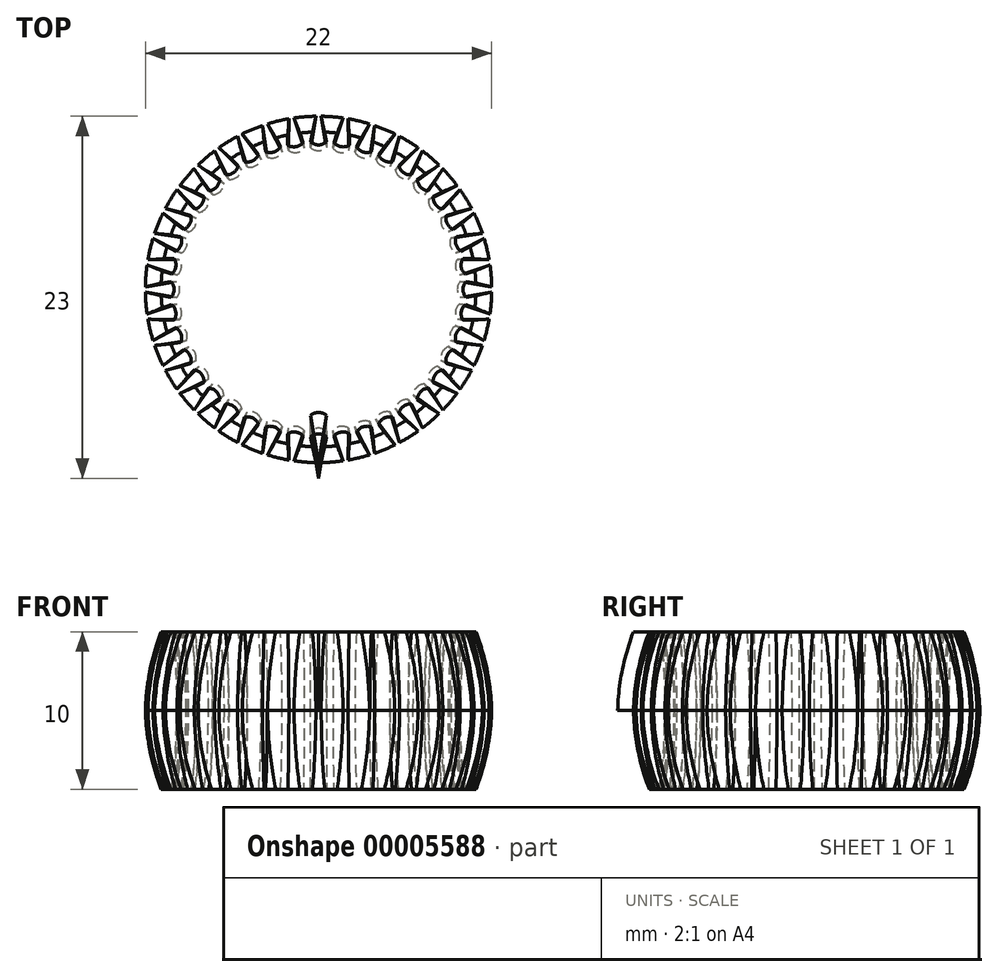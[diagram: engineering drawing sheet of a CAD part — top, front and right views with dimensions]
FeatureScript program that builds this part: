
annotation { "Feature Type Name" : "Feature", "Feature Type Description" : "" }
export const myFeature = defineFeature(function(context is Context, id is Id, definition is map)
    precondition{}
    {
        {
            var Q0;
            Q0=qCreatedBy(makeId("Right.planeOp"),FACE);
            var sketch = newSketch(context, id + "F0", { "sketchPlane" : qUnion([Q0])});
            skLineSegment(sketch, "E0.bottom", {"start": v(0, 5) * mm, "end": v(-10, 5) * mm});
            skLineSegment(sketch, "E0.left", {"start": v(0, 5) * mm, "end": v(0, 0) * mm});
            skLineSegment(sketch, "E1", {"start": v(-10, 5) * mm, "end": v(-10, 0) * mm, "construction": true});
            skArc(sketch, "E2", {"start": v(-10, 5) * mm, "mid": v(-10.71, 2.54) * mm, "end": v(-11, 0) * mm});
            skPoint(sketch, "E2.third.point", {"position": v(13.48, -12.02) * mm});
            skLineSegment(sketch, "E3", {"start": v(-11, 0) * mm, "end": v(0, 0) * mm});
            skSolve(sketch);
        }
        {
            var Q0;
            Q0=makeQuery(id+"F0.imprint","IMPRINT",FACE,{"disambiguationData":[TD([[makeQuery(id+"F0.imprint","IMPRINT",EDGE,{"derivedFrom":sQuery(id+"F0.wireOp",EDGE,"E0.bottom")}),1.0]])]});
            var Q1;
            Q1=sQuery(id+"F0.wireOp",EDGE,"E0.left");
            revolve(context, id + "F1", {"entities" : qUnion([Q0]), "axis" : qUnion([Q1]), "revolveType" : RevolveType.FULL});
        }
        {
            var Q0;
            Q0=qCreatedBy(makeId("Top.planeOp"),FACE);
            var sketch = newSketch(context, id + "F2", { "sketchPlane" : qUnion([Q0])});
            skLineSegment(sketch, "E4", {"start": v(0, -12) * mm, "end": v(-0.5, -9) * mm});
            skLineSegment(sketch, "E5", {"start": v(-0.5, -9) * mm, "end": v(0, -9) * mm});
            skLineSegment(sketch, "E6.0.MirrorCS", {"start": v(0, -12) * mm, "end": v(0.5, -9) * mm});
            skLineSegment(sketch, "E6.1.MirrorCS", {"start": v(0.5, -9) * mm, "end": v(0, -9) * mm});
            skLineSegment(sketch, "E7", {"start": v(0, 0) * mm, "end": v(0, -12) * mm, "construction": true});
            skLineSegment(sketch, "E8", {"start": v(0, -12) * mm, "end": v(0, -9) * mm, "construction": true});
            skArc(sketch, "E9", {"start": v(0.5, -9) * mm, "mid": v(0, -8.81) * mm, "end": v(-0.5, -9) * mm});
            skSolve(sketch);
        }
        {
            var Q0;
            Q0=qCreatedBy(makeId("Right.planeOp"),FACE);
            var sketch = newSketch(context, id + "F3", { "sketchPlane" : qUnion([Q0])});
            skFitSpline(sketch, "E10", {"points": [v(-9.63, 0) * mm, v(-10, 5) * mm], "startDerivative": vector(-0.08, 3.63) * mm, "endDerivative": vector(-0.92, 4.07) * mm});
            skSolve(sketch);
        }
        {
            var Q0;
            Q0 = qSketchRegion(id + "F2", true);
            var Q1;
            Q1=sQuery(id+"F0.wireOp",EDGE,"E2");
            sweep(context, id + "F4", {"profiles" : qUnion([Q0]), "path" : qUnion([Q1]), "keepProfileOrientation" : true});
        }
        {
            var Q0;
            Q0=qCreatedBy(makeId("Right.planeOp"),FACE);
            var sketch = newSketch(context, id + "F5", { "sketchPlane" : qUnion([Q0])});
            skLineSegment(sketch, "E11", {"start": v(0, 0) * mm, "end": v(0, 14.13) * mm, "construction": true});
            skSolve(sketch);
        }
        {
            var Q0;
            Q0 = qSketchRegion(id + "F2", true);
            var Q1;
            Q1 = qBodyType(qCreatedBy(id + "F3" ,EDGE), BodyType.WIRE);
            sweep(context, id + "F6", {"profiles" : qUnion([Q0]), "path" : qUnion([Q1]), "keepProfileOrientation" : true});
        }
        {
            var Q0;
            Q0=makeQuery(id+"F4.opSweep","SWEPT_FACE",FACE,{"disambiguationData":[OSD([sQuery(id+"F0.wireOp",EDGE,"E2"),sQuery(id+"F2.wireOp",EDGE,"E6.0.MirrorCS")])]});
            var Q1;
            Q1=makeQuery(id+"F6.opSweep","SWEPT_BODY",BODY,{"disambiguationData":[OSD([sQuery(id+"F0.wireOp",EDGE,"E1"),sQuery(id+"F2.wireOp",EDGE,"E4"),sQuery(id+"F2.wireOp",EDGE,"E6.0.MirrorCS"),sQuery(id+"F2.wireOp",EDGE,"E9")])]});
            var Q2;
            Q2=sQuery(id+"F5.wireOp",EDGE,"E11");
            circularPattern(context, id + "F7", {"entities" : qUnion([Q1]), "axis" : qUnion([Q2]), "angle" : 360 * degree, "instanceCount" : 40, "equalSpace" : true});
        }
        {
            var Q0;
            Q0=makeQuery(id+"F7.opPattern","COPY",BODY,{"derivedFrom":makeQuery(id+"F6.opSweep","SWEPT_BODY",BODY,{"disambiguationData":[OSD([sQuery(id+"F0.wireOp",EDGE,"E1"),sQuery(id+"F2.wireOp",EDGE,"E4"),sQuery(id+"F2.wireOp",EDGE,"E6.0.MirrorCS"),sQuery(id+"F2.wireOp",EDGE,"E9")])]}),"instanceName":"22"});
            var Q1;
            Q1=makeQuery(id+"F7.opPattern","COPY",BODY,{"derivedFrom":makeQuery(id+"F6.opSweep","SWEPT_BODY",BODY,{"disambiguationData":[OSD([sQuery(id+"F0.wireOp",EDGE,"E1"),sQuery(id+"F2.wireOp",EDGE,"E4"),sQuery(id+"F2.wireOp",EDGE,"E6.0.MirrorCS"),sQuery(id+"F2.wireOp",EDGE,"E9")])]}),"instanceName":"18"});
            var Q2;
            Q2=makeQuery(id+"F7.opPattern","COPY",BODY,{"derivedFrom":makeQuery(id+"F6.opSweep","SWEPT_BODY",BODY,{"disambiguationData":[OSD([sQuery(id+"F0.wireOp",EDGE,"E1"),sQuery(id+"F2.wireOp",EDGE,"E4"),sQuery(id+"F2.wireOp",EDGE,"E6.0.MirrorCS"),sQuery(id+"F2.wireOp",EDGE,"E9")])]}),"instanceName":"43"});
            var Q3;
            Q3=makeQuery(id+"F7.opPattern","COPY",BODY,{"derivedFrom":makeQuery(id+"F6.opSweep","SWEPT_BODY",BODY,{"disambiguationData":[OSD([sQuery(id+"F0.wireOp",EDGE,"E1"),sQuery(id+"F2.wireOp",EDGE,"E4"),sQuery(id+"F2.wireOp",EDGE,"E6.0.MirrorCS"),sQuery(id+"F2.wireOp",EDGE,"E9")])]}),"instanceName":"26"});
            var Q4;
            Q4=makeQuery(id+"F7.opPattern","COPY",BODY,{"derivedFrom":makeQuery(id+"F6.opSweep","SWEPT_BODY",BODY,{"disambiguationData":[OSD([sQuery(id+"F0.wireOp",EDGE,"E1"),sQuery(id+"F2.wireOp",EDGE,"E4"),sQuery(id+"F2.wireOp",EDGE,"E6.0.MirrorCS"),sQuery(id+"F2.wireOp",EDGE,"E9")])]}),"instanceName":"35"});
            var Q5;
            Q5=makeQuery(id+"F7.opPattern","COPY",BODY,{"derivedFrom":makeQuery(id+"F6.opSweep","SWEPT_BODY",BODY,{"disambiguationData":[OSD([sQuery(id+"F0.wireOp",EDGE,"E1"),sQuery(id+"F2.wireOp",EDGE,"E4"),sQuery(id+"F2.wireOp",EDGE,"E6.0.MirrorCS"),sQuery(id+"F2.wireOp",EDGE,"E9")])]}),"instanceName":"15"});
            var Q6;
            Q6=makeQuery(id+"F7.opPattern","COPY",BODY,{"derivedFrom":makeQuery(id+"F6.opSweep","SWEPT_BODY",BODY,{"disambiguationData":[OSD([sQuery(id+"F0.wireOp",EDGE,"E1"),sQuery(id+"F2.wireOp",EDGE,"E4"),sQuery(id+"F2.wireOp",EDGE,"E6.0.MirrorCS"),sQuery(id+"F2.wireOp",EDGE,"E9")])]}),"instanceName":"25"});
            var Q7;
            Q7=makeQuery(id+"F7.opPattern","COPY",BODY,{"derivedFrom":makeQuery(id+"F6.opSweep","SWEPT_BODY",BODY,{"disambiguationData":[OSD([sQuery(id+"F0.wireOp",EDGE,"E1"),sQuery(id+"F2.wireOp",EDGE,"E4"),sQuery(id+"F2.wireOp",EDGE,"E6.0.MirrorCS"),sQuery(id+"F2.wireOp",EDGE,"E9")])]}),"instanceName":"39"});
            var Q8;
            Q8=makeQuery(id+"F7.opPattern","COPY",BODY,{"derivedFrom":makeQuery(id+"F6.opSweep","SWEPT_BODY",BODY,{"disambiguationData":[OSD([sQuery(id+"F0.wireOp",EDGE,"E1"),sQuery(id+"F2.wireOp",EDGE,"E4"),sQuery(id+"F2.wireOp",EDGE,"E6.0.MirrorCS"),sQuery(id+"F2.wireOp",EDGE,"E9")])]}),"instanceName":"42"});
            var Q9;
            Q9=makeQuery(id+"F7.opPattern","COPY",BODY,{"derivedFrom":makeQuery(id+"F6.opSweep","SWEPT_BODY",BODY,{"disambiguationData":[OSD([sQuery(id+"F0.wireOp",EDGE,"E1"),sQuery(id+"F2.wireOp",EDGE,"E4"),sQuery(id+"F2.wireOp",EDGE,"E6.0.MirrorCS"),sQuery(id+"F2.wireOp",EDGE,"E9")])]}),"instanceName":"40"});
            var Q10;
            Q10=makeQuery(id+"F7.opPattern","COPY",BODY,{"derivedFrom":makeQuery(id+"F6.opSweep","SWEPT_BODY",BODY,{"disambiguationData":[OSD([sQuery(id+"F0.wireOp",EDGE,"E1"),sQuery(id+"F2.wireOp",EDGE,"E4"),sQuery(id+"F2.wireOp",EDGE,"E6.0.MirrorCS"),sQuery(id+"F2.wireOp",EDGE,"E9")])]}),"instanceName":"16"});
            var Q11;
            Q11=makeQuery(id+"F7.opPattern","COPY",BODY,{"derivedFrom":makeQuery(id+"F6.opSweep","SWEPT_BODY",BODY,{"disambiguationData":[OSD([sQuery(id+"F0.wireOp",EDGE,"E1"),sQuery(id+"F2.wireOp",EDGE,"E4"),sQuery(id+"F2.wireOp",EDGE,"E6.0.MirrorCS"),sQuery(id+"F2.wireOp",EDGE,"E9")])]}),"instanceName":"33"});
            var Q12;
            Q12=makeQuery(id+"F7.opPattern","COPY",BODY,{"derivedFrom":makeQuery(id+"F6.opSweep","SWEPT_BODY",BODY,{"disambiguationData":[OSD([sQuery(id+"F0.wireOp",EDGE,"E1"),sQuery(id+"F2.wireOp",EDGE,"E4"),sQuery(id+"F2.wireOp",EDGE,"E6.0.MirrorCS"),sQuery(id+"F2.wireOp",EDGE,"E9")])]}),"instanceName":"45"});
            var Q13;
            Q13=makeQuery(id+"F7.opPattern","COPY",BODY,{"derivedFrom":makeQuery(id+"F6.opSweep","SWEPT_BODY",BODY,{"disambiguationData":[OSD([sQuery(id+"F0.wireOp",EDGE,"E1"),sQuery(id+"F2.wireOp",EDGE,"E4"),sQuery(id+"F2.wireOp",EDGE,"E6.0.MirrorCS"),sQuery(id+"F2.wireOp",EDGE,"E9")])]}),"instanceName":"32"});
            var Q14;
            Q14=makeQuery(id+"F7.opPattern","COPY",BODY,{"derivedFrom":makeQuery(id+"F6.opSweep","SWEPT_BODY",BODY,{"disambiguationData":[OSD([sQuery(id+"F0.wireOp",EDGE,"E1"),sQuery(id+"F2.wireOp",EDGE,"E4"),sQuery(id+"F2.wireOp",EDGE,"E6.0.MirrorCS"),sQuery(id+"F2.wireOp",EDGE,"E9")])]}),"instanceName":"4"});
            var Q15;
            Q15=makeQuery(id+"F7.opPattern","COPY",BODY,{"derivedFrom":makeQuery(id+"F6.opSweep","SWEPT_BODY",BODY,{"disambiguationData":[OSD([sQuery(id+"F0.wireOp",EDGE,"E1"),sQuery(id+"F2.wireOp",EDGE,"E4"),sQuery(id+"F2.wireOp",EDGE,"E6.0.MirrorCS"),sQuery(id+"F2.wireOp",EDGE,"E9")])]}),"instanceName":"29"});
            var Q16;
            Q16=makeQuery(id+"F7.opPattern","COPY",BODY,{"derivedFrom":makeQuery(id+"F6.opSweep","SWEPT_BODY",BODY,{"disambiguationData":[OSD([sQuery(id+"F0.wireOp",EDGE,"E1"),sQuery(id+"F2.wireOp",EDGE,"E4"),sQuery(id+"F2.wireOp",EDGE,"E6.0.MirrorCS"),sQuery(id+"F2.wireOp",EDGE,"E9")])]}),"instanceName":"7"});
            var Q17;
            Q17=makeQuery(id+"F7.opPattern","COPY",BODY,{"derivedFrom":makeQuery(id+"F6.opSweep","SWEPT_BODY",BODY,{"disambiguationData":[OSD([sQuery(id+"F0.wireOp",EDGE,"E1"),sQuery(id+"F2.wireOp",EDGE,"E4"),sQuery(id+"F2.wireOp",EDGE,"E6.0.MirrorCS"),sQuery(id+"F2.wireOp",EDGE,"E9")])]}),"instanceName":"14"});
            var Q18;
            Q18=makeQuery(id+"F7.opPattern","COPY",BODY,{"derivedFrom":makeQuery(id+"F6.opSweep","SWEPT_BODY",BODY,{"disambiguationData":[OSD([sQuery(id+"F0.wireOp",EDGE,"E1"),sQuery(id+"F2.wireOp",EDGE,"E4"),sQuery(id+"F2.wireOp",EDGE,"E6.0.MirrorCS"),sQuery(id+"F2.wireOp",EDGE,"E9")])]}),"instanceName":"48"});
            var Q19;
            Q19=makeQuery(id+"F7.opPattern","COPY",BODY,{"derivedFrom":makeQuery(id+"F6.opSweep","SWEPT_BODY",BODY,{"disambiguationData":[OSD([sQuery(id+"F0.wireOp",EDGE,"E1"),sQuery(id+"F2.wireOp",EDGE,"E4"),sQuery(id+"F2.wireOp",EDGE,"E6.0.MirrorCS"),sQuery(id+"F2.wireOp",EDGE,"E9")])]}),"instanceName":"11"});
            var Q20;
            Q20=makeQuery(id+"F7.opPattern","COPY",BODY,{"derivedFrom":makeQuery(id+"F6.opSweep","SWEPT_BODY",BODY,{"disambiguationData":[OSD([sQuery(id+"F0.wireOp",EDGE,"E1"),sQuery(id+"F2.wireOp",EDGE,"E4"),sQuery(id+"F2.wireOp",EDGE,"E6.0.MirrorCS"),sQuery(id+"F2.wireOp",EDGE,"E9")])]}),"instanceName":"12"});
            var Q21;
            Q21=makeQuery(id+"F7.opPattern","COPY",BODY,{"derivedFrom":makeQuery(id+"F6.opSweep","SWEPT_BODY",BODY,{"disambiguationData":[OSD([sQuery(id+"F0.wireOp",EDGE,"E1"),sQuery(id+"F2.wireOp",EDGE,"E4"),sQuery(id+"F2.wireOp",EDGE,"E6.0.MirrorCS"),sQuery(id+"F2.wireOp",EDGE,"E9")])]}),"instanceName":"37"});
            var Q22;
            Q22=makeQuery(id+"F7.opPattern","COPY",BODY,{"derivedFrom":makeQuery(id+"F6.opSweep","SWEPT_BODY",BODY,{"disambiguationData":[OSD([sQuery(id+"F0.wireOp",EDGE,"E1"),sQuery(id+"F2.wireOp",EDGE,"E4"),sQuery(id+"F2.wireOp",EDGE,"E6.0.MirrorCS"),sQuery(id+"F2.wireOp",EDGE,"E9")])]}),"instanceName":"44"});
            var Q23;
            Q23=makeQuery(id+"F6.opSweep","SWEPT_BODY",BODY,{"disambiguationData":[OSD([sQuery(id+"F0.wireOp",EDGE,"E1"),sQuery(id+"F2.wireOp",EDGE,"E4"),sQuery(id+"F2.wireOp",EDGE,"E6.0.MirrorCS"),sQuery(id+"F2.wireOp",EDGE,"E9")])]});
            var Q24;
            Q24=makeQuery(id+"F7.opPattern","COPY",BODY,{"derivedFrom":makeQuery(id+"F6.opSweep","SWEPT_BODY",BODY,{"disambiguationData":[OSD([sQuery(id+"F0.wireOp",EDGE,"E1"),sQuery(id+"F2.wireOp",EDGE,"E4"),sQuery(id+"F2.wireOp",EDGE,"E6.0.MirrorCS"),sQuery(id+"F2.wireOp",EDGE,"E9")])]}),"instanceName":"9"});
            var Q25;
            Q25=makeQuery(id+"F7.opPattern","COPY",BODY,{"derivedFrom":makeQuery(id+"F6.opSweep","SWEPT_BODY",BODY,{"disambiguationData":[OSD([sQuery(id+"F0.wireOp",EDGE,"E1"),sQuery(id+"F2.wireOp",EDGE,"E4"),sQuery(id+"F2.wireOp",EDGE,"E6.0.MirrorCS"),sQuery(id+"F2.wireOp",EDGE,"E9")])]}),"instanceName":"10"});
            var Q26;
            Q26=makeQuery(id+"F7.opPattern","COPY",BODY,{"derivedFrom":makeQuery(id+"F6.opSweep","SWEPT_BODY",BODY,{"disambiguationData":[OSD([sQuery(id+"F0.wireOp",EDGE,"E1"),sQuery(id+"F2.wireOp",EDGE,"E4"),sQuery(id+"F2.wireOp",EDGE,"E6.0.MirrorCS"),sQuery(id+"F2.wireOp",EDGE,"E9")])]}),"instanceName":"20"});
            var Q27;
            Q27=makeQuery(id+"F7.opPattern","COPY",BODY,{"derivedFrom":makeQuery(id+"F6.opSweep","SWEPT_BODY",BODY,{"disambiguationData":[OSD([sQuery(id+"F0.wireOp",EDGE,"E1"),sQuery(id+"F2.wireOp",EDGE,"E4"),sQuery(id+"F2.wireOp",EDGE,"E6.0.MirrorCS"),sQuery(id+"F2.wireOp",EDGE,"E9")])]}),"instanceName":"47"});
            var Q28;
            Q28=makeQuery(id+"F7.opPattern","COPY",BODY,{"derivedFrom":makeQuery(id+"F6.opSweep","SWEPT_BODY",BODY,{"disambiguationData":[OSD([sQuery(id+"F0.wireOp",EDGE,"E1"),sQuery(id+"F2.wireOp",EDGE,"E4"),sQuery(id+"F2.wireOp",EDGE,"E6.0.MirrorCS"),sQuery(id+"F2.wireOp",EDGE,"E9")])]}),"instanceName":"6"});
            var Q29;
            Q29=makeQuery(id+"F7.opPattern","COPY",BODY,{"derivedFrom":makeQuery(id+"F6.opSweep","SWEPT_BODY",BODY,{"disambiguationData":[OSD([sQuery(id+"F0.wireOp",EDGE,"E1"),sQuery(id+"F2.wireOp",EDGE,"E4"),sQuery(id+"F2.wireOp",EDGE,"E6.0.MirrorCS"),sQuery(id+"F2.wireOp",EDGE,"E9")])]}),"instanceName":"41"});
            var Q30;
            Q30=makeQuery(id+"F7.opPattern","COPY",BODY,{"derivedFrom":makeQuery(id+"F6.opSweep","SWEPT_BODY",BODY,{"disambiguationData":[OSD([sQuery(id+"F0.wireOp",EDGE,"E1"),sQuery(id+"F2.wireOp",EDGE,"E4"),sQuery(id+"F2.wireOp",EDGE,"E6.0.MirrorCS"),sQuery(id+"F2.wireOp",EDGE,"E9")])]}),"instanceName":"8"});
            var Q31;
            Q31=makeQuery(id+"F7.opPattern","COPY",BODY,{"derivedFrom":makeQuery(id+"F6.opSweep","SWEPT_BODY",BODY,{"disambiguationData":[OSD([sQuery(id+"F0.wireOp",EDGE,"E1"),sQuery(id+"F2.wireOp",EDGE,"E4"),sQuery(id+"F2.wireOp",EDGE,"E6.0.MirrorCS"),sQuery(id+"F2.wireOp",EDGE,"E9")])]}),"instanceName":"2"});
            var Q32;
            Q32=makeQuery(id+"F7.opPattern","COPY",BODY,{"derivedFrom":makeQuery(id+"F6.opSweep","SWEPT_BODY",BODY,{"disambiguationData":[OSD([sQuery(id+"F0.wireOp",EDGE,"E1"),sQuery(id+"F2.wireOp",EDGE,"E4"),sQuery(id+"F2.wireOp",EDGE,"E6.0.MirrorCS"),sQuery(id+"F2.wireOp",EDGE,"E9")])]}),"instanceName":"21"});
            var Q33;
            Q33=makeQuery(id+"F7.opPattern","COPY",BODY,{"derivedFrom":makeQuery(id+"F6.opSweep","SWEPT_BODY",BODY,{"disambiguationData":[OSD([sQuery(id+"F0.wireOp",EDGE,"E1"),sQuery(id+"F2.wireOp",EDGE,"E4"),sQuery(id+"F2.wireOp",EDGE,"E6.0.MirrorCS"),sQuery(id+"F2.wireOp",EDGE,"E9")])]}),"instanceName":"27"});
            var Q34;
            Q34=makeQuery(id+"F7.opPattern","COPY",BODY,{"derivedFrom":makeQuery(id+"F6.opSweep","SWEPT_BODY",BODY,{"disambiguationData":[OSD([sQuery(id+"F0.wireOp",EDGE,"E1"),sQuery(id+"F2.wireOp",EDGE,"E4"),sQuery(id+"F2.wireOp",EDGE,"E6.0.MirrorCS"),sQuery(id+"F2.wireOp",EDGE,"E9")])]}),"instanceName":"34"});
            var Q35;
            Q35=makeQuery(id+"F7.opPattern","COPY",BODY,{"derivedFrom":makeQuery(id+"F6.opSweep","SWEPT_BODY",BODY,{"disambiguationData":[OSD([sQuery(id+"F0.wireOp",EDGE,"E1"),sQuery(id+"F2.wireOp",EDGE,"E4"),sQuery(id+"F2.wireOp",EDGE,"E6.0.MirrorCS"),sQuery(id+"F2.wireOp",EDGE,"E9")])]}),"instanceName":"36"});
            var Q36;
            Q36=makeQuery(id+"F7.opPattern","COPY",BODY,{"derivedFrom":makeQuery(id+"F6.opSweep","SWEPT_BODY",BODY,{"disambiguationData":[OSD([sQuery(id+"F0.wireOp",EDGE,"E1"),sQuery(id+"F2.wireOp",EDGE,"E4"),sQuery(id+"F2.wireOp",EDGE,"E6.0.MirrorCS"),sQuery(id+"F2.wireOp",EDGE,"E9")])]}),"instanceName":"3"});
            var Q37;
            Q37=makeQuery(id+"F7.opPattern","COPY",BODY,{"derivedFrom":makeQuery(id+"F6.opSweep","SWEPT_BODY",BODY,{"disambiguationData":[OSD([sQuery(id+"F0.wireOp",EDGE,"E1"),sQuery(id+"F2.wireOp",EDGE,"E4"),sQuery(id+"F2.wireOp",EDGE,"E6.0.MirrorCS"),sQuery(id+"F2.wireOp",EDGE,"E9")])]}),"instanceName":"17"});
            var Q38;
            Q38=makeQuery(id+"F7.opPattern","COPY",BODY,{"derivedFrom":makeQuery(id+"F6.opSweep","SWEPT_BODY",BODY,{"disambiguationData":[OSD([sQuery(id+"F0.wireOp",EDGE,"E1"),sQuery(id+"F2.wireOp",EDGE,"E4"),sQuery(id+"F2.wireOp",EDGE,"E6.0.MirrorCS"),sQuery(id+"F2.wireOp",EDGE,"E9")])]}),"instanceName":"1"});
            var Q39;
            Q39=makeQuery(id+"F7.opPattern","COPY",BODY,{"derivedFrom":makeQuery(id+"F6.opSweep","SWEPT_BODY",BODY,{"disambiguationData":[OSD([sQuery(id+"F0.wireOp",EDGE,"E1"),sQuery(id+"F2.wireOp",EDGE,"E4"),sQuery(id+"F2.wireOp",EDGE,"E6.0.MirrorCS"),sQuery(id+"F2.wireOp",EDGE,"E9")])]}),"instanceName":"38"});
            var Q40;
            Q40=makeQuery(id+"F7.opPattern","COPY",BODY,{"derivedFrom":makeQuery(id+"F6.opSweep","SWEPT_BODY",BODY,{"disambiguationData":[OSD([sQuery(id+"F0.wireOp",EDGE,"E1"),sQuery(id+"F2.wireOp",EDGE,"E4"),sQuery(id+"F2.wireOp",EDGE,"E6.0.MirrorCS"),sQuery(id+"F2.wireOp",EDGE,"E9")])]}),"instanceName":"31"});
            var Q41;
            Q41=makeQuery(id+"F7.opPattern","COPY",BODY,{"derivedFrom":makeQuery(id+"F6.opSweep","SWEPT_BODY",BODY,{"disambiguationData":[OSD([sQuery(id+"F0.wireOp",EDGE,"E1"),sQuery(id+"F2.wireOp",EDGE,"E4"),sQuery(id+"F2.wireOp",EDGE,"E6.0.MirrorCS"),sQuery(id+"F2.wireOp",EDGE,"E9")])]}),"instanceName":"24"});
            var Q42;
            Q42=makeQuery(id+"F7.opPattern","COPY",BODY,{"derivedFrom":makeQuery(id+"F6.opSweep","SWEPT_BODY",BODY,{"disambiguationData":[OSD([sQuery(id+"F0.wireOp",EDGE,"E1"),sQuery(id+"F2.wireOp",EDGE,"E4"),sQuery(id+"F2.wireOp",EDGE,"E6.0.MirrorCS"),sQuery(id+"F2.wireOp",EDGE,"E9")])]}),"instanceName":"28"});
            var Q43;
            Q43=makeQuery(id+"F7.opPattern","COPY",BODY,{"derivedFrom":makeQuery(id+"F6.opSweep","SWEPT_BODY",BODY,{"disambiguationData":[OSD([sQuery(id+"F0.wireOp",EDGE,"E1"),sQuery(id+"F2.wireOp",EDGE,"E4"),sQuery(id+"F2.wireOp",EDGE,"E6.0.MirrorCS"),sQuery(id+"F2.wireOp",EDGE,"E9")])]}),"instanceName":"5"});
            var Q44;
            Q44=makeQuery(id+"F7.opPattern","COPY",BODY,{"derivedFrom":makeQuery(id+"F6.opSweep","SWEPT_BODY",BODY,{"disambiguationData":[OSD([sQuery(id+"F0.wireOp",EDGE,"E1"),sQuery(id+"F2.wireOp",EDGE,"E4"),sQuery(id+"F2.wireOp",EDGE,"E6.0.MirrorCS"),sQuery(id+"F2.wireOp",EDGE,"E9")])]}),"instanceName":"13"});
            var Q45;
            Q45=makeQuery(id+"F7.opPattern","COPY",BODY,{"derivedFrom":makeQuery(id+"F6.opSweep","SWEPT_BODY",BODY,{"disambiguationData":[OSD([sQuery(id+"F0.wireOp",EDGE,"E1"),sQuery(id+"F2.wireOp",EDGE,"E4"),sQuery(id+"F2.wireOp",EDGE,"E6.0.MirrorCS"),sQuery(id+"F2.wireOp",EDGE,"E9")])]}),"instanceName":"30"});
            var Q46;
            Q46=makeQuery(id+"F7.opPattern","COPY",BODY,{"derivedFrom":makeQuery(id+"F6.opSweep","SWEPT_BODY",BODY,{"disambiguationData":[OSD([sQuery(id+"F0.wireOp",EDGE,"E1"),sQuery(id+"F2.wireOp",EDGE,"E4"),sQuery(id+"F2.wireOp",EDGE,"E6.0.MirrorCS"),sQuery(id+"F2.wireOp",EDGE,"E9")])]}),"instanceName":"46"});
            var Q47;
            Q47=makeQuery(id+"F7.opPattern","COPY",BODY,{"derivedFrom":makeQuery(id+"F6.opSweep","SWEPT_BODY",BODY,{"disambiguationData":[OSD([sQuery(id+"F0.wireOp",EDGE,"E1"),sQuery(id+"F2.wireOp",EDGE,"E4"),sQuery(id+"F2.wireOp",EDGE,"E6.0.MirrorCS"),sQuery(id+"F2.wireOp",EDGE,"E9")])]}),"instanceName":"19"});
            var Q48;
            Q48=makeQuery(id+"F7.opPattern","COPY",BODY,{"derivedFrom":makeQuery(id+"F6.opSweep","SWEPT_BODY",BODY,{"disambiguationData":[OSD([sQuery(id+"F0.wireOp",EDGE,"E1"),sQuery(id+"F2.wireOp",EDGE,"E4"),sQuery(id+"F2.wireOp",EDGE,"E6.0.MirrorCS"),sQuery(id+"F2.wireOp",EDGE,"E9")])]}),"instanceName":"49"});
            var Q49;
            Q49=makeQuery(id+"F7.opPattern","COPY",BODY,{"derivedFrom":makeQuery(id+"F6.opSweep","SWEPT_BODY",BODY,{"disambiguationData":[OSD([sQuery(id+"F0.wireOp",EDGE,"E1"),sQuery(id+"F2.wireOp",EDGE,"E4"),sQuery(id+"F2.wireOp",EDGE,"E6.0.MirrorCS"),sQuery(id+"F2.wireOp",EDGE,"E9")])]}),"instanceName":"23"});
            var Q50;
            Q50=makeQuery(id+"F1.opRevolve","SWEPT_BODY",BODY,{"disambiguationData":[OSD([sQuery(id+"F0.wireOp",EDGE,"E0.bottom"),sQuery(id+"F0.wireOp",EDGE,"E0.left"),sQuery(id+"F0.wireOp",EDGE,"E2"),sQuery(id+"F0.wireOp",EDGE,"E3")])]});
            booleanBodies(context, id + "F8", {"operationType" : BooleanOperationType.SUBTRACTION, "tools" : qUnion([Q0, Q1, Q2, Q3, Q4, Q5, Q6, Q7, Q8, Q9, Q10, Q11, Q12, Q13, Q14, Q15, Q16, Q17, Q18, Q19, Q20, Q21, Q22, Q23, Q24, Q25, Q26, Q27, Q28, Q29, Q30, Q31, Q32, Q33, Q34, Q35, Q36, Q37, Q38, Q39, Q40, Q41, Q42, Q43, Q44, Q45, Q46, Q47, Q48, Q49]), "targets" : qUnion([Q50])});
        }
        {
            var Q0;
            Q0=makeQuery(id+"F1.opRevolve","SWEPT_BODY",BODY,{"disambiguationData":[OSD([sQuery(id+"F0.wireOp",EDGE,"E0.bottom"),sQuery(id+"F0.wireOp",EDGE,"E0.left"),sQuery(id+"F0.wireOp",EDGE,"E2"),sQuery(id+"F0.wireOp",EDGE,"E3")])]});
            var Q1;
            Q1=qCreatedBy(makeId("Top.planeOp"),FACE);
            mirror(context, id + "F9", {"entities" : qUnion([Q0]), "mirrorPlane" : qUnion([Q1])});
        }
    });
